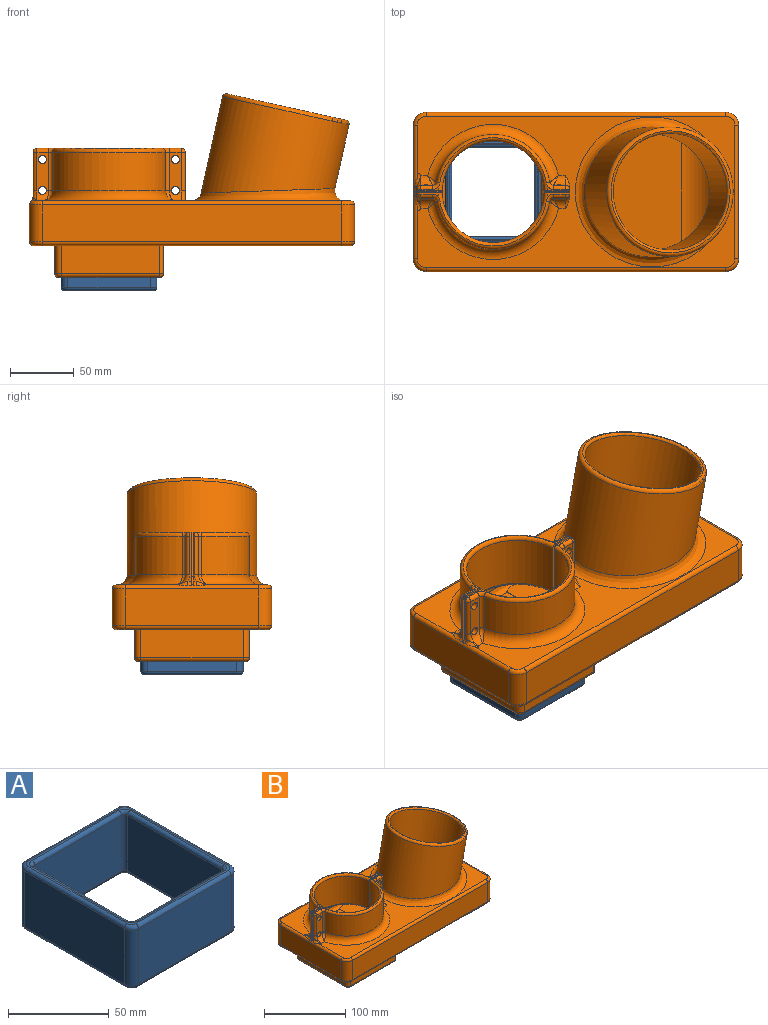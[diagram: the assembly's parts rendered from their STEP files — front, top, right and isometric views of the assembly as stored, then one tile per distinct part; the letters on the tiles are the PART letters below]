
ASSEMBLY  parts=2 mates=1
PART A: 50 faces, bbox 75.8x80.8x38 mm
  f0: plane 76x71mm, normal (0,0,1), area 296mm2, adj f22,f23,f24,f25,f26,f27,f28,f29
  f1: plane 61x34mm, normal (0,-1,0), area 2074mm2, adj f36,f37,f45,f46
  f2: plane 66x34mm, normal (-1,0,0), area 2244mm2, adj f35,f44,f45,f49
  f3: plane 61x34mm, normal (0,1,0), area 2074mm2, adj f33,f34,f43,f44
  f4: plane 66x34mm, normal (1,0,0), area 2244mm2, adj f30,f33,f37,f38
  f5: cylinder r=5mm len=34mm, axis (0,0,-1), area 267mm2, adj f6,f12,f20,f27
  f6: plane 65x34mm, normal (0,1,0), area 2210mm2, adj f5,f7,f18,f25
  f7: cylinder r=5mm len=34mm, axis (0,0,1), area 267mm2, adj f6,f8,f16,f23
  f8: plane 70x34mm, normal (1,0,0), area 2380mm2, adj f7,f9,f14,f22
  f9: cylinder r=5mm len=34mm, axis (0,0,1), area 267mm2, adj f8,f10,f15,f24
  f10: plane 65x34mm, normal (0,-1,0), area 2210mm2, adj f9,f11,f17,f26
  f11: cylinder r=5mm len=34mm, axis (0,0,-1), area 267mm2, adj f10,f12,f19,f28
  f12: plane 70x34mm, normal (-1,0,0), area 2380mm2, adj f5,f11,f21,f29
  f13: plane 76x71mm, normal (0,0,-1), area 296mm2, adj f14,f15,f16,f17,f18,f19,f20,f21
  f14: cylinder r=2mm len=70mm, axis (0,1,0), area 219.9mm2, adj f8,f13,f15,f16
  f15: torus R=3mm, axis (0,0,-1), area 21.1mm2, adj f9,f13,f14,f17
  f16: torus R=3mm, axis (0,0,-1), area 21.1mm2, adj f7,f13,f14,f18
  f17: cylinder r=2mm len=65mm, axis (-1,0,0), area 204.2mm2, adj f10,f13,f15,f19
  f18: cylinder r=2mm len=65mm, axis (1,0,0), area 204.2mm2, adj f6,f13,f16,f20
  f19: torus R=3mm, axis (0,0,-1), area 21.1mm2, adj f11,f13,f17,f21
  f20: torus R=3mm, axis (0,0,-1), area 21.1mm2, adj f5,f13,f18,f21
  f21: cylinder r=2mm len=70mm, axis (0,1,0), area 219.9mm2, adj f12,f13,f19,f20
  f22: cylinder r=2mm len=70mm, axis (0,1,0), area 219.9mm2, adj f0,f8,f23,f24
  f23: torus R=3mm, axis (0,0,-1), area 21.1mm2, adj f0,f7,f22,f25
  f24: torus R=3mm, axis (0,0,-1), area 21.1mm2, adj f0,f9,f22,f26
  f25: cylinder r=2mm len=65mm, axis (1,0,0), area 204.2mm2, adj f0,f6,f23,f27
  f26: cylinder r=2mm len=65mm, axis (-1,0,0), area 204.2mm2, adj f0,f10,f24,f28
  f27: torus R=3mm, axis (0,0,-1), area 21.1mm2, adj f0,f5,f25,f29
  f28: torus R=3mm, axis (0,0,-1), area 21.1mm2, adj f0,f11,f26,f29
  f29: cylinder r=2mm len=70mm, axis (0,1,0), area 219.9mm2, adj f0,f12,f27,f28
  f30: cylinder r=2mm len=66mm, axis (0,-1,0), area 207.3mm2, adj f4,f13,f31,f32
  f31: torus R=4mm, axis (0,0,-1), area 13.5mm2, adj f13,f30,f33,f34
  f32: torus R=4mm, axis (0,0,-1), area 13.5mm2, adj f13,f30,f36,f37
  f33: cylinder r=2mm len=34mm, axis (0,0,1), area 106.8mm2, adj f3,f4,f31,f39
  f34: cylinder r=2mm len=61mm, axis (1,0,0), area 191.6mm2, adj f3,f13,f31,f40
  f35: cylinder r=2mm len=66mm, axis (0,-1,0), area 207.3mm2, adj f2,f13,f40,f41
  f36: cylinder r=2mm len=61mm, axis (-1,0,0), area 191.6mm2, adj f1,f13,f32,f41
  f37: cylinder r=2mm len=34mm, axis (0,0,1), area 106.8mm2, adj f1,f4,f32,f42
  f38: cylinder r=2mm len=66mm, axis (0,-1,0), area 207.3mm2, adj f0,f4,f39,f42
  f39: torus R=4mm, axis (0,0,-1), area 13.5mm2, adj f0,f33,f38,f43
  f40: torus R=4mm, axis (0,0,-1), area 13.5mm2, adj f13,f34,f35,f44
  f41: torus R=4mm, axis (0,0,-1), area 13.5mm2, adj f13,f35,f36,f45
  f42: torus R=4mm, axis (0,0,-1), area 13.5mm2, adj f0,f37,f38,f46
  f43: cylinder r=2mm len=61mm, axis (1,0,0), area 191.6mm2, adj f0,f3,f39,f47
  f44: cylinder r=2mm len=34mm, axis (0,0,-1), area 106.8mm2, adj f2,f3,f40,f47
  f45: cylinder r=2mm len=34mm, axis (0,0,-1), area 106.8mm2, adj f1,f2,f41,f48
  f46: cylinder r=2mm len=61mm, axis (-1,0,0), area 191.6mm2, adj f0,f1,f42,f48
  f47: torus R=4mm, axis (0,0,-1), area 13.5mm2, adj f0,f43,f44,f49
  f48: torus R=4mm, axis (0,0,-1), area 13.5mm2, adj f0,f45,f46,f49
  f49: cylinder r=2mm len=66mm, axis (0,-1,0), area 207.3mm2, adj f0,f2,f47,f48
PART B: 183 faces, bbox 257.5x127.5x145.7 mm
  f0: plane 224.1x20mm, normal (0,-1,0), area 4133.6mm2, adj f3,f48,f60,f165,f166,f167
  f1: plane 224.1x20mm, normal (0,1,0), area 4133.6mm2, adj f4,f48,f58,f165,f166,f167
  f2: plane 105x93.5mm, normal (0,0,1), area 2369mm2, adj f3,f4,f6,f7,f143,f147,f150,f151
  f3: cylinder r=5mm len=148.6mm, axis (1,0,0), area 891.1mm2, adj f0,f2,f142,f164,f165
  f4: cylinder r=5mm len=148.6mm, axis (-1,0,0), area 891.1mm2, adj f1,f2,f144,f164,f165
  f5: cylinder r=5mm len=70mm, axis (0,-1,0), area 442.9mm2, adj f6,f7,f62,f164
  f6: torus R=10mm, axis (0,0,1), area 80.1mm2, adj f2,f5,f145,f147,f164
  f7: torus R=10mm, axis (0,0,1), area 80.1mm2, adj f2,f5,f146,f150,f164
  f8: plane 7x7mm, normal (0,0,-1), area 10.5mm2, adj f91,f96,f159
  f9: plane 7x7mm, normal (0,0,-1), area 10.5mm2, adj f88,f91,f160
  f10: plane 7x7mm, normal (0,0,-1), area 9.7mm2, adj f93,f95,f96,f155
  f11: plane 13.91x3.35mm, normal (0,0,1), area 20.5mm2, adj f21,f22,f130,f133,f134
  f12: plane 13.91x3.25mm, normal (0,0,1), area 19.2mm2, adj f34,f38,f115,f116,f119
  f13: plane 35.17x2.45mm, normal (-1,0,0), area 47.6mm2, adj f21,f22,f121,f123,f138
  f14: cylinder r=39.95mm len=79.9mm, axis (0,0,1), area 10245.7mm2, adj f22,f23,f28,f29,f38,f39,f115,f133
  f15: plane 38.28x4.75mm, normal (1,0,0), area 58.3mm2, adj f20,f23,f29,f120,f122
  f16: plane 30.28x9.39mm, normal (0,1,0), area 235.4mm2, adj f24,f25,f97,f122,f128,f129
  f17: cylinder r=44.95mm len=88.64mm, axis (0,0,1), area 3819mm2, adj f98,f128,f131,f135
  f18: plane 30.28x9.39mm, normal (0,1,0), area 235.4mm2, adj f26,f27,f99,f123,f130,f131
  f19: plane 13.91x3.35mm, normal (0,0,1), area 20.5mm2, adj f20,f23,f129,f132,f133
  f20: cylinder r=3mm len=3mm, axis (0,1,0), area 6.1mm2, adj f15,f19,f23,f125
  f21: cylinder r=3mm len=3mm, axis (0,-1,0), area 6.1mm2, adj f11,f13,f22,f126
  f22: plane 42.01x21.52mm, normal (0,-1,0), area 748.4mm2, adj f11,f13,f14,f21,f26,f27,f28,f44
  f23: plane 41.3x19.75mm, normal (0,-1,0), area 747mm2, adj f14,f15,f19,f20,f24,f25,f29,f133
  f24: cylinder r=3.17mm len=6.35mm, axis (0,-1,0), area 85.8mm2, adj f16,f23
  f25: cylinder r=3.17mm len=6.35mm, axis (0,-1,0), area 85.8mm2, adj f16,f23,f97
  f26: cylinder r=3.17mm len=6.35mm, axis (0,-1,0), area 85.8mm2, adj f18,f22
  f27: cylinder r=3.17mm len=6.35mm, axis (0,-1,0), area 85.8mm2, adj f18,f22,f99
  f28: plane 19.56x1.5mm, normal (0,0,1), area 29.3mm2, adj f14,f22,f39,f44
  f29: plane 249.86x119.86mm, normal (0,0,1), area 9320.7mm2, adj f14,f15,f23,f30,f38,f44,f72,f73
  f30: plane 38.28x4.65mm, normal (1,0,0), area 54.5mm2, adj f29,f34,f38,f106,f109
  f31: plane 35.17x2.35mm, normal (-1,0,0), area 44mm2, adj f33,f39,f104,f105,f140
  f32: plane 13.91x3.25mm, normal (0,0,1), area 19.2mm2, adj f33,f39,f111,f114,f115
  f33: cylinder r=3mm len=3mm, axis (0,-1,0), area 5.7mm2, adj f31,f32,f39,f108
  f34: cylinder r=3mm len=3mm, axis (0,1,0), area 5.7mm2, adj f12,f30,f38,f112
  f35: plane 30.28x9.39mm, normal (0,-1,0), area 235.4mm2, adj f40,f41,f102,f105,f110,f111
  f36: cylinder r=44.95mm len=88.64mm, axis (0,0,1), area 3819mm2, adj f101,f110,f117,f118
  f37: plane 30.28x9.39mm, normal (0,-1,0), area 235.4mm2, adj f42,f43,f100,f109,f116,f117
  f38: plane 41.3x19.75mm, normal (0,1,0), area 747.1mm2, adj f12,f14,f29,f30,f34,f42,f43,f115
  f39: plane 42.01x21.52mm, normal (0,1,0), area 748.4mm2, adj f14,f28,f31,f32,f33,f40,f41,f44
  f40: cylinder r=3.17mm len=6.35mm, axis (0,-1,0), area 83.8mm2, adj f35,f39
  f41: cylinder r=3.17mm len=6.35mm, axis (0,-1,0), area 83.8mm2, adj f35,f39,f102
  f42: cylinder r=3.17mm len=6.35mm, axis (0,-1,0), area 83.8mm2, adj f37,f38
  f43: cylinder r=3.17mm len=6.35mm, axis (0,-1,0), area 86.4mm2, adj f37,f38,f100
  f44: cylinder r=3mm len=105mm, axis (0,1,0), area 463.9mm2, adj f22,f28,f29,f39,f52,f74,f77,f137
  f45: cylinder r=45.8mm len=107.53mm, axis (-0.22,0,-0.98), area 21137.6mm2, adj f47,f163
  f46: cylinder r=50.8mm len=115.92mm, axis (-0.22,0,-0.98), area 20510.5mm2, adj f103,f136
  f47: extruded ~93.82x91.6mm, area 582.5mm2, adj f45,f141
  f48: plane 229.1x115mm, normal (0,0,-1), area 13172.6mm2, adj f0,f1,f58,f59,f60,f141,f162,f167
  f49: plane 249x119mm, normal (0,0,-1), area 21953.5mm2, adj f64,f65,f66,f67,f68,f69,f79,f80
  f50: plane 235x29mm, normal (0,-1,0), area 6815mm2, adj f51,f57,f72,f79
  f51: cylinder r=10mm len=29mm, axis (0,0,1), area 455.5mm2, adj f50,f52,f74,f81
  f52: plane 105x29mm, normal (-1,0,0), area 3045mm2, adj f44,f51,f53,f83
  f53: cylinder r=10mm len=29mm, axis (0,0,1), area 455.5mm2, adj f52,f54,f77,f85
  f54: plane 235x29mm, normal (0,1,0), area 6815mm2, adj f53,f55,f78,f86
  f55: cylinder r=10mm len=29mm, axis (0,0,1), area 455.5mm2, adj f54,f56,f76,f84
  f56: plane 105x29mm, normal (1,0,0), area 3045mm2, adj f55,f57,f75,f82
  f57: cylinder r=10mm len=29mm, axis (0,0,1), area 455.5mm2, adj f50,f56,f73,f80
  f58: cylinder r=5mm len=20mm, axis (0,0,1), area 157.1mm2, adj f1,f48,f59,f144
  f59: plane 105x20mm, normal (1,0,0), area 2100mm2, adj f48,f58,f60,f143
  f60: cylinder r=5mm len=20mm, axis (0,0,1), area 157.1mm2, adj f0,f48,f59,f142
  f61: plane 65x23mm, normal (0,-1,0), area 1495mm2, adj f145,f147,f148,f157
  f62: plane 70x23mm, normal (-1,0,0), area 1610mm2, adj f5,f145,f146,f161
  f63: plane 65x23mm, normal (0,1,0), area 1495mm2, adj f146,f149,f150,f158
  f64: plane 84x22mm, normal (1,0,0), area 1848mm2, adj f49,f87,f91,f92
  f65: plane 77x22mm, normal (0,1,0), area 1694mm2, adj f49,f66,f92,f96
  f66: cylinder r=5mm len=22mm, axis (0,0,1), area 172.8mm2, adj f49,f65,f67,f95
  f67: plane 80x22mm, normal (-1,0,0), area 1760mm2, adj f49,f66,f68,f93
  f68: cylinder r=5mm len=22mm, axis (0,0,1), area 172.8mm2, adj f49,f67,f69,f90
  f69: plane 77x22mm, normal (0,-1,0), area 1694mm2, adj f49,f68,f87,f88
  f70: plane 70x23mm, normal (1,0,0), area 1610mm2, adj f148,f149,f153,f154
  f71: plane 7x7mm, normal (0,0,-1), area 9.7mm2, adj f88,f90,f93,f156
  f72: cylinder r=3mm len=235mm, axis (-1,0,0), area 1107.4mm2, adj f29,f50,f73,f74
  f73: torus R=7mm, axis (0,0,-1), area 66mm2, adj f29,f57,f72,f75
  f74: torus R=7mm, axis (0,0,-1), area 66mm2, adj f29,f44,f51,f72
  f75: cylinder r=3mm len=105mm, axis (0,-1,0), area 494.8mm2, adj f29,f56,f73,f76
  f76: torus R=7mm, axis (0,0,-1), area 66mm2, adj f29,f55,f75,f78
  f77: torus R=7mm, axis (0,0,-1), area 66mm2, adj f29,f44,f53,f78
  f78: cylinder r=3mm len=235mm, axis (1,0,0), area 1107.4mm2, adj f29,f54,f76,f77
  f79: cylinder r=3mm len=235mm, axis (1,0,0), area 1107.4mm2, adj f49,f50,f80,f81
  f80: torus R=7mm, axis (0,0,-1), area 66mm2, adj f49,f57,f79,f82
  f81: torus R=7mm, axis (0,0,-1), area 66mm2, adj f49,f51,f79,f83
  f82: cylinder r=3mm len=105mm, axis (0,1,0), area 494.8mm2, adj f49,f56,f80,f84
  f83: cylinder r=3mm len=105mm, axis (0,-1,0), area 494.8mm2, adj f49,f52,f81,f85
  f84: torus R=7mm, axis (0,0,-1), area 66mm2, adj f49,f55,f82,f86
  f85: torus R=7mm, axis (0,0,-1), area 66mm2, adj f49,f53,f83,f86
  f86: cylinder r=3mm len=235mm, axis (-1,0,0), area 1107.4mm2, adj f49,f54,f84,f85
  f87: cylinder r=3mm len=22mm, axis (0,0,-1), area 103.7mm2, adj f49,f64,f69,f89
  f88: cylinder r=3mm len=77mm, axis (-1,0,0), area 362.9mm2, adj f9,f69,f71,f89,f90,f158
  f89: sphere r=3mm, area 14.1mm2, adj f87,f88,f91
  f90: torus R=2mm, axis (0,0,1), area 28.9mm2, adj f68,f71,f88,f93
  f91: cylinder r=3mm len=84mm, axis (0,-1,0), area 395.8mm2, adj f8,f9,f64,f89,f94,f161
  f92: cylinder r=3mm len=22mm, axis (0,0,-1), area 103.7mm2, adj f49,f64,f65,f94
  f93: cylinder r=3mm len=80mm, axis (0,1,0), area 377mm2, adj f10,f67,f71,f90,f95,f154
  f94: sphere r=3mm, area 9mm2, adj f91,f92,f96
  f95: torus R=2mm, axis (0,0,1), area 28.9mm2, adj f10,f66,f93,f96
  f96: cylinder r=3mm len=77mm, axis (1,0,0), area 362.9mm2, adj f8,f10,f65,f94,f95,f157
  f97: cylinder r=8mm len=9.39mm, axis (-1,0,0), area 84.7mm2, adj f16,f25,f29,f120,f124
  f98: torus R=52.95mm, axis (0,0,-1), area 1637.9mm2, adj f17,f29,f124,f127
  f99: cylinder r=8mm len=9.39mm, axis (-1,0,0), area 84.7mm2, adj f18,f27,f29,f121,f127
  f100: cylinder r=8mm len=9.39mm, axis (1,0,0), area 84.7mm2, adj f29,f37,f43,f106,f113
  f101: torus R=52.95mm, axis (0,0,-1), area 1637.9mm2, adj f29,f36,f107,f113
  f102: cylinder r=8mm len=9.39mm, axis (-1,0,0), area 84.7mm2, adj f29,f35,f41,f104,f107
  f103: bspline ~120.33x117.54mm, area 4295.9mm2, adj f29,f46
  f104: torus R=11mm, axis (-1,0,0), area 35mm2, adj f29,f31,f102,f105,f139
  f105: cylinder r=3mm len=30.28mm, axis (0,0,1), area 142.7mm2, adj f31,f35,f104,f108
  f106: torus R=11mm, axis (-1,0,0), area 50.2mm2, adj f29,f30,f100,f109
  f107: bspline ~8.66x8.01mm, area 23.7mm2, adj f101,f102,f110
  f108: sphere r=3mm, area 9mm2, adj f33,f105,f111
  f109: cylinder r=3mm len=30.28mm, axis (0,0,-1), area 142.7mm2, adj f30,f37,f106,f112
  f110: cylinder r=3mm len=30.28mm, axis (0,0,1), area 127.4mm2, adj f35,f36,f107,f114
  f111: cylinder r=3mm len=9.39mm, axis (1,0,0), area 44.3mm2, adj f32,f35,f108,f114
  f112: sphere r=3mm, area 19.3mm2, adj f34,f109,f116
  f113: bspline ~8.66x8.01mm, area 23.7mm2, adj f100,f101,f117
  f114: torus R=6mm, axis (0,0,1), area 26.2mm2, adj f32,f110,f111,f115,f118
  f115: torus R=42.95mm, axis (0,0,1), area 538.3mm2, adj f12,f14,f32,f38,f39,f114,f118,f119
  f116: cylinder r=3mm len=9.39mm, axis (1,0,0), area 44.3mm2, adj f12,f37,f112,f119
  f117: cylinder r=3mm len=30.28mm, axis (0,0,1), area 127.4mm2, adj f36,f37,f113,f119
  f118: torus R=41.95mm, axis (0,0,1), area 520.5mm2, adj f36,f114,f115,f119
  f119: torus R=6mm, axis (0,0,1), area 26.2mm2, adj f12,f115,f116,f117,f118
  f120: torus R=11mm, axis (1,0,0), area 50.2mm2, adj f15,f29,f97,f122
  f121: torus R=11mm, axis (1,0,0), area 35mm2, adj f13,f29,f99,f123,f137
  f122: cylinder r=3mm len=30.28mm, axis (0,0,-1), area 142.7mm2, adj f15,f16,f120,f125
  f123: cylinder r=3mm len=30.28mm, axis (0,0,1), area 142.7mm2, adj f13,f18,f121,f126
  f124: bspline ~8.66x8.01mm, area 23.7mm2, adj f97,f98,f128
  f125: sphere r=3mm, area 9mm2, adj f20,f122,f129
  f126: sphere r=3mm, area 14.1mm2, adj f21,f123,f130
  f127: bspline ~8.66x8.01mm, area 23.7mm2, adj f98,f99,f131
  f128: cylinder r=3mm len=30.28mm, axis (0,0,1), area 127.4mm2, adj f16,f17,f124,f132
  f129: cylinder r=3mm len=9.39mm, axis (-1,0,0), area 44.3mm2, adj f16,f19,f125,f132
  f130: cylinder r=3mm len=9.39mm, axis (-1,0,0), area 44.3mm2, adj f11,f18,f126,f134
  f131: cylinder r=3mm len=30.28mm, axis (0,0,1), area 127.4mm2, adj f17,f18,f127,f134
  f132: torus R=6mm, axis (0,0,1), area 26.2mm2, adj f19,f128,f129,f133,f135
  f133: torus R=42.95mm, axis (0,0,1), area 539.3mm2, adj f11,f14,f19,f22,f23,f132,f134,f135
  f134: torus R=6mm, axis (0,0,1), area 26.2mm2, adj f11,f130,f131,f133,f135
  f135: torus R=41.95mm, axis (0,0,1), area 520.5mm2, adj f17,f132,f133,f134
  f136: torus R=47.8mm, axis (0.22,0,0.98), area 1471.8mm2, adj f46,f163
  f137: bspline ~15.88x4.24mm, area 35.3mm2, adj f29,f44,f121,f138
  f138: cylinder r=5mm len=3.82mm, axis (0,1,0), area 10.6mm2, adj f13,f22,f44,f137
  f139: bspline ~15.88x4.24mm, area 35.3mm2, adj f29,f44,f104,f140
  f140: cylinder r=5mm len=3.82mm, axis (0,1,0), area 10.2mm2, adj f31,f39,f44,f139
  f141: bspline ~99.84x97.62mm, area 1404.7mm2, adj f47,f48,f168
  f142: sphere r=5mm, area 53.5mm2, adj f3,f60,f143
  f143: cylinder r=5mm len=105mm, axis (0,1,0), area 824.7mm2, adj f2,f59,f142,f144
  f144: sphere r=5mm, area 39.3mm2, adj f4,f58,f143
  f145: cylinder r=5mm len=23mm, axis (0,0,1), area 180.6mm2, adj f6,f61,f62,f159
  f146: cylinder r=5mm len=23mm, axis (0,0,1), area 180.6mm2, adj f7,f62,f63,f160
  f147: cylinder r=5mm len=65mm, axis (1,0,0), area 510.5mm2, adj f2,f6,f61,f151
  f148: cylinder r=5mm len=23mm, axis (0,0,-1), area 180.6mm2, adj f61,f70,f151,f155
  f149: cylinder r=5mm len=23mm, axis (0,0,-1), area 180.6mm2, adj f63,f70,f152,f156
  f150: cylinder r=5mm len=65mm, axis (-1,0,0), area 510.5mm2, adj f2,f7,f63,f152
  f151: torus R=10mm, axis (0,0,1), area 84.1mm2, adj f2,f147,f148,f153
  f152: torus R=10mm, axis (0,0,1), area 84.1mm2, adj f2,f149,f150,f153
  f153: cylinder r=5mm len=70mm, axis (0,1,0), area 549.8mm2, adj f2,f70,f151,f152
  f154: cylinder r=2mm len=70mm, axis (0,-1,0), area 219.9mm2, adj f70,f93,f155,f156
  f155: torus R=7mm, axis (0,0,1), area 28.3mm2, adj f10,f148,f154,f157
  f156: torus R=7mm, axis (0,0,1), area 28.3mm2, adj f71,f149,f154,f158
  f157: cylinder r=2mm len=65mm, axis (-1,0,0), area 204.2mm2, adj f61,f96,f155,f159
  f158: cylinder r=2mm len=65mm, axis (1,0,0), area 204.2mm2, adj f63,f88,f156,f160
  f159: torus R=7mm, axis (0,0,1), area 28.3mm2, adj f8,f145,f157,f161
  f160: torus R=7mm, axis (0,0,1), area 28.3mm2, adj f9,f146,f158,f161
  f161: cylinder r=2mm len=70mm, axis (0,1,0), area 219.9mm2, adj f62,f91,f159,f160
  f162: torus R=41.95mm, axis (0,0,-1), area 802.9mm2, adj f14,f48
  f163: torus R=47.8mm, axis (0.22,0,0.98), area 918.4mm2, adj f45,f136
  f164: plane 106.42x1.06mm, normal (-1,0,0), area 18.4mm2, adj f2,f3,f4,f5,f6,f7,f165
  f165: plane 115x106.99mm, normal (-0.09,0,1), area 12235.8mm2, adj f0,f1,f3,f4,f164,f166
  f166: cylinder r=30mm len=115mm, axis (0,-1,0), area 3103.2mm2, adj f0,f1,f165,f167
  f167: plane 115x1.89mm, normal (-0.84,0,0.55), area 259.8mm2, adj f0,f1,f48,f166,f168
  f168: plane 21.51x1.24mm, normal (0,0,1), area 17.6mm2, adj f141,f167
  f169: plane 115x71.11mm, normal (0.09,0,-1), area 8089.6mm2, adj f170,f177,f178,f179,f180,f181
  f170: plane 115x18.66mm, normal (0.86,0,-0.51), area 2491.2mm2, adj f169,f180,f181,f182
  f171: plane 105x20mm, normal (-1,0,0), area 2100mm2, adj f172,f173,f174,f182
  f172: cylinder r=5mm len=20mm, axis (0,0,1), area 157.1mm2, adj f171,f175,f181,f182
  f173: cylinder r=5mm len=20mm, axis (0,0,1), area 157.1mm2, adj f171,f176,f180,f182
  f174: cylinder r=5mm len=105mm, axis (0,-1,0), area 824.7mm2, adj f171,f175,f176,f179
  f175: sphere r=5mm, area 25mm2, adj f172,f174,f178
  f176: sphere r=5mm, area 39.3mm2, adj f173,f174,f177
  f177: cylinder r=5mm len=85.48mm, axis (-1,0,0), area 511.2mm2, adj f169,f176,f179,f180
  f178: cylinder r=5mm len=85.48mm, axis (1,0,0), area 511.2mm2, adj f169,f175,f179,f181
  f179: plane 105x85.48mm, normal (0,0,1), area 8975.8mm2, adj f169,f174,f177,f178
  f180: plane 29.36x20mm, normal (0,1,0), area 194.8mm2, adj f169,f170,f173,f177,f182
  f181: plane 29.36x20mm, normal (0,-1,0), area 194.8mm2, adj f169,f170,f172,f178,f182
  f182: plane 115x8.37mm, normal (0,0,-1), area 952.2mm2, adj f170,f171,f172,f173,f180,f181
PLACE A t=(2.56,13.85,3)mm
PLACE B t=(2.56,13.85,0)mm
MATE slider A.f11 <-> B.f149  axis (0,0,-1) through (-29.94,-21.15,-92.28)mm
